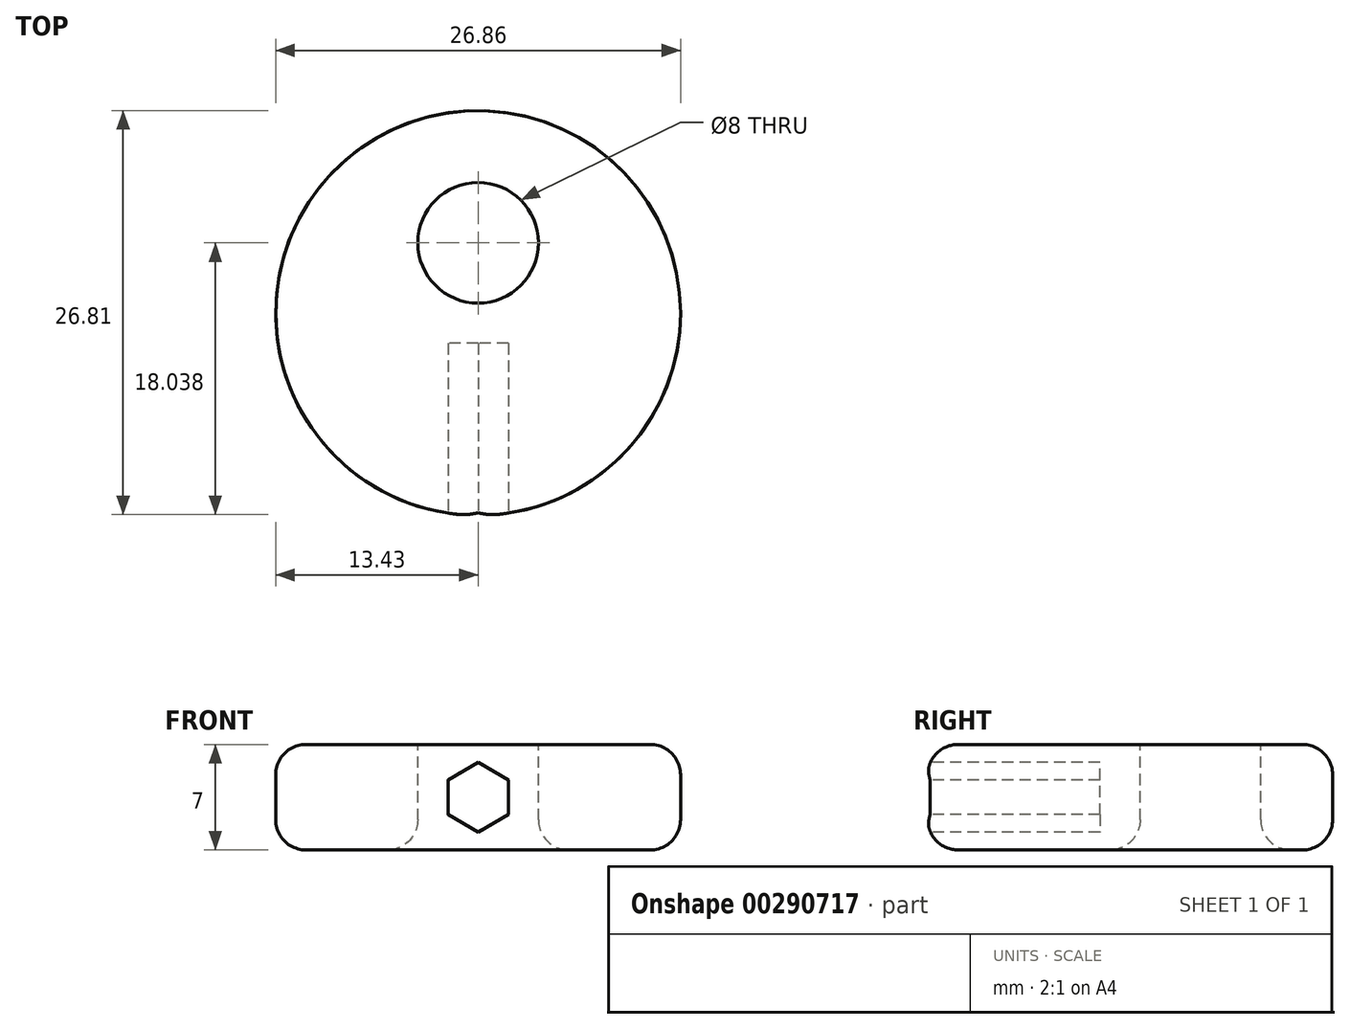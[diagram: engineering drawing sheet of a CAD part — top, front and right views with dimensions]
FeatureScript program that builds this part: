
annotation { "Feature Type Name" : "Feature", "Feature Type Description" : "" }
export const myFeature = defineFeature(function(context is Context, id is Id, definition is map)
    precondition{}
    {
        {
            var Q0;
            Q0=qCreatedBy(makeId("Top.planeOp"),FACE);
            var sketch = newSketch(context, id + "F0", { "sketchPlane" : qUnion([Q0])});
            skCircle(sketch, "E0", {"center": v(0, 0) * mm, "radius": 13.43 * mm});
            skSolve(sketch);
        }
        {
            var Q0;
            Q0 = qSketchRegion(id + "F0", true);
            extrude(context, id + "F1", {"entities" : qUnion([Q0]), "flatOperationType" : FlatOperationType.REMOVE, "offsetDistance" : 25 * mm, "depth" : 7 * mm, "domain" : OperationDomain.MODEL, "symmetric" : true});
        }
        {
            var Q0;
            Q0=qCreatedBy(makeId("Front.planeOp"),FACE);
            cPlane(context, id + "F2", {"entities" : qUnion([Q0]), "cplaneType" : CPlaneType.OFFSET, "offset" : 60 * mm, "width" : 150 * mm, "height" : 150 * mm});
        }
        {
            var Q0;
            Q0=qCreatedBy(id+"F2.planeOp",FACE);
            var sketch = newSketch(context, id + "F3", { "sketchPlane" : qUnion([Q0]), "disableImprinting" : false});
            skPoint(sketch, "E1.0.midPoint", {"position": v(1.26, -0.72) * mm});
            skCircle(sketch, "E2.cCircle", {"center": v(0, 0) * mm, "radius": 2 * mm, "construction": true});
            skLineSegment(sketch, "E2.seed", {"start": v(2, 1.15) * mm, "end": v(0, 2.3) * mm});
            skLineSegment(sketch, "E2.pattern.0.1.0", {"start": v(0, 2.3) * mm, "end": v(-2, 1.15) * mm});
            skLineSegment(sketch, "E2.pattern.0.2.0", {"start": v(-2, 1.15) * mm, "end": v(-2, -1.15) * mm});
            skLineSegment(sketch, "E2.pattern.0.3.0", {"start": v(-2, -1.15) * mm, "end": v(0, -2.3) * mm});
            skLineSegment(sketch, "E2.pattern.0.4.0", {"start": v(0, -2.3) * mm, "end": v(2, -1.15) * mm});
            skLineSegment(sketch, "E2.pattern.0.5.0", {"start": v(2, -1.15) * mm, "end": v(2, 1.15) * mm});
            skPoint(sketch, "E2.midPoint", {"position": v(1, 1.73) * mm, "construction": true});
            skSolve(sketch);
        }
        {
            var Q0;
            Q0 = qSketchRegion(id + "F3", true);
            extrude(context, id + "F4", {"entities" : qUnion([Q0]), "operationType" : NewBodyOperationType.REMOVE, "oppositeDirection" : true, "offsetDistance" : 25 * mm, "depth" : 58 * mm});
        }
        {
            var Q0;
            Q0=makeQuery(id+"F1.opExtrude","CAP_FACE",FACE,{"disambiguationData":[OSD([sQuery(id+"F0.wireOp",EDGE,"E0")])],"isStart":false});
            var sketch = newSketch(context, id + "F5", { "sketchPlane" : qUnion([Q0])});
            skCircle(sketch, "E3", {"center": v(0, 4.66) * mm, "radius": 4 * mm});
            skSolve(sketch);
        }
        {
            var Q0;
            Q0 = qSketchRegion(id + "F5", true);
            extrude(context, id + "F6", {"entities" : qUnion([Q0]), "operationType" : NewBodyOperationType.REMOVE, "oppositeDirection" : true, "offsetDistance" : 25 * mm, "depth" : 25 * mm});
        }
        {
            var Q0;
            Q0=makeQuery(id+"F1.opExtrude","CAP_EDGE",EDGE,{"disambiguationData":[OSD([sQuery(id+"F0.wireOp",EDGE,"E0")])],"isStart":false});
            var Q1;
            Q1=makeQuery(id+"F1.opExtrude","CAP_EDGE",EDGE,{"disambiguationData":[OSD([sQuery(id+"F0.wireOp",EDGE,"E0")])],"isStart":true});
            var Q2;
            Q2=makeQuery(id+"F6.boolean.opBoolean","COPY",EDGE,{"derivedFrom":makeQuery(id+"F6.opExtrude","CAP_EDGE",EDGE,{"disambiguationData":[OSD([sQuery(id+"F5.wireOp",EDGE,"E3")])],"isStart":true})});
            var Q3;
            Q3=makeQuery(id+"F6.boolean.opBoolean","INTERSECT",EDGE,{"derivedFrom":[makeQuery(id+"F1.opExtrude","CAP_FACE",FACE,{"disambiguationData":[OSD([sQuery(id+"F0.wireOp",EDGE,"E0")])],"isStart":true}),makeQuery(id+"F6.opExtrude","SWEPT_FACE",FACE,{"disambiguationData":[OSD([sQuery(id+"F5.wireOp",EDGE,"E3")])]})]});
            fillet(context, id + "F7", {"entities" : qUnion([Q0, Q1, Q2, Q3]), "radius" : 2 * mm, "tangentPropagation" : true, "allowEdgeOverflow" : false});
        }
    });
